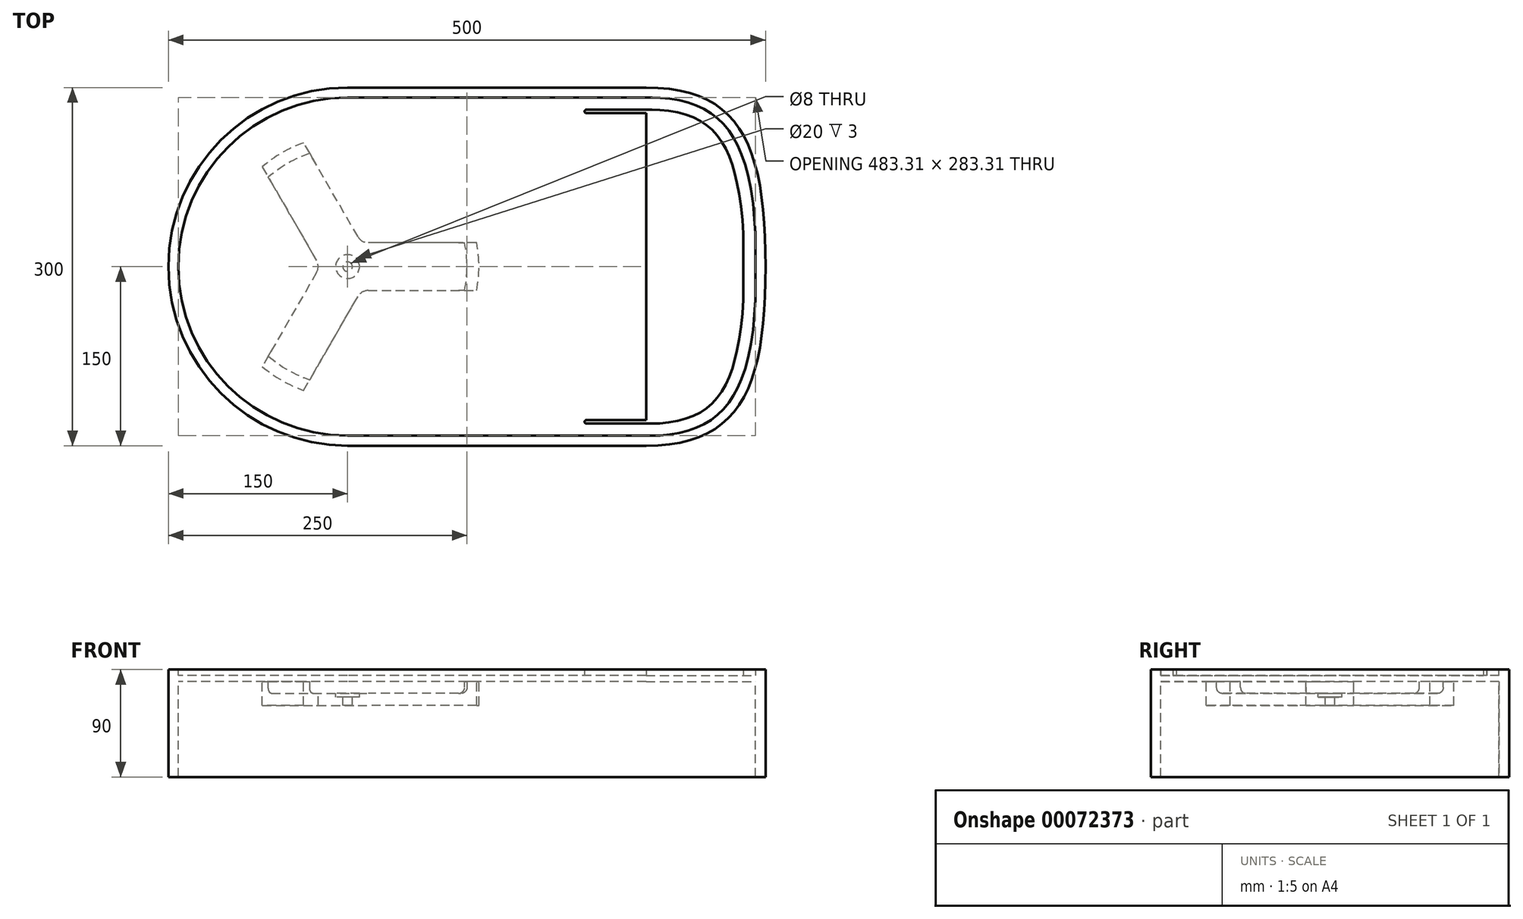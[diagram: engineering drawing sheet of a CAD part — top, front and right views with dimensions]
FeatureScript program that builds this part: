
annotation { "Feature Type Name" : "Feature", "Feature Type Description" : "" }
export const myFeature = defineFeature(function(context is Context, id is Id, definition is map)
    precondition{}
    {
        {
            var Q0;
            Q0=qCreatedBy(makeId("Top.planeOp"),FACE);
            var sketch = newSketch(context, id + "F0", { "sketchPlane" : qUnion([Q0])});
            skLineSegment(sketch, "E0.top", {"start": v(0, 150) * mm, "end": v(-250, 150) * mm});
            skArc(sketch, "E1", {"start": v(-250, 150) * mm, "mid": v(-356.07, 106.07) * mm, "end": v(-400, 0) * mm});
            skPoint(sketch, "E2", {"position": v(100, 0) * mm});
            skLineSegment(sketch, "E3", {"start": v(100, 0) * mm, "end": v(100, 200) * mm, "construction": true});
            skFitSpline(sketch, "E4", {"points": [v(0, 150) * mm, v(100, 0) * mm], "startDerivative": vector(240, 0) * mm, "endDerivative": vector(0, -300) * mm});
            skLineSegment(sketch, "E5", {"start": v(0, 150) * mm, "end": v(265.73, 150) * mm, "construction": true});
            skLineSegment(sketch, "E6", {"start": v(-400, 0) * mm, "end": v(100, 0) * mm, "construction": true});
            skArc(sketch, "E7.MirrorCS", {"start": v(-250, -150) * mm, "mid": v(-356.07, -106.07) * mm, "end": v(-400, 0) * mm});
            skLineSegment(sketch, "E8.MirrorCS", {"start": v(0, -150) * mm, "end": v(-250, -150) * mm});
            skFitSpline(sketch, "E9.MirrorCS", {"points": [v(0, -150) * mm, v(100, 0) * mm], "startDerivative": vector(240, 0) * mm, "endDerivative": vector(0, 300) * mm});
            skCircle(sketch, "E10", {"center": v(-250, 0) * mm, "radius": 110 * mm});
            skLineSegment(sketch, "E11.0", {"start": v(0, 130) * mm, "end": v(-250, 130) * mm, "construction": true});
            skFitSpline(sketch, "E11.1", {"points": [v(0, -130) * mm, v(4.48, -130) * mm, v(12.87, -129.65) * mm, v(23.79, -128.15) * mm, v(33.11, -125.8) * mm, v(40.98, -122.68) * mm, v(47.63, -118.88) * mm, v(53.34, -114.36) * mm, v(58.4, -108.95) * mm, v(62.93, -102.43) * mm, v(67, -94.6) * mm, v(70.55, -85.38) * mm, v(73.56, -74.7) * mm, v(76, -62.57) * mm, v(77.84, -49.03) * mm, v(79.54, -29.12) * mm, v(80, -12.17) * mm, v(80, 0) * mm], "construction": true});
            skLineSegment(sketch, "E11.2", {"start": v(0, -130) * mm, "end": v(-250, -130) * mm, "construction": true});
            skFitSpline(sketch, "E11.3", {"points": [v(0, 130) * mm, v(4.48, 130) * mm, v(12.87, 129.65) * mm, v(23.79, 128.15) * mm, v(33.11, 125.8) * mm, v(40.98, 122.68) * mm, v(47.63, 118.88) * mm, v(53.34, 114.36) * mm, v(58.4, 108.95) * mm, v(62.93, 102.43) * mm, v(67, 94.6) * mm, v(70.55, 85.38) * mm, v(73.56, 74.7) * mm, v(76, 62.57) * mm, v(77.84, 49.03) * mm, v(79.54, 29.12) * mm, v(80, 12.17) * mm, v(80, 0) * mm], "construction": true});
            skArc(sketch, "E11.4", {"start": v(-250, -130) * mm, "mid": v(-341.92, -91.92) * mm, "end": v(-380, 0) * mm, "construction": true});
            skArc(sketch, "E11.5", {"start": v(-250, 130) * mm, "mid": v(-341.92, 91.92) * mm, "end": v(-380, 0) * mm, "construction": true});
            skLineSegment(sketch, "E12", {"start": v(0, 130) * mm, "end": v(-50, 130) * mm, "construction": true});
            skLineSegment(sketch, "E13", {"start": v(-50, -150) * mm, "end": v(-50, 150) * mm, "construction": true});
            skLineSegment(sketch, "E14", {"start": v(-50, -130) * mm, "end": v(0, -130) * mm, "construction": true});
            skCircle(sketch, "E15", {"center": v(-250, 0) * mm, "radius": 100 * mm});
            skLineSegment(sketch, "E16.0", {"start": v(0, 141.65) * mm, "end": v(-250, 141.65) * mm});
            skFitSpline(sketch, "E16.1", {"points": [v(0, -141.65) * mm, v(4.78, -141.65) * mm, v(13.84, -141.28) * mm, v(25.94, -139.63) * mm, v(36.62, -136.94) * mm, v(45.99, -133.25) * mm, v(54.15, -128.6) * mm, v(61.28, -122.95) * mm, v(67.52, -116.25) * mm, v(72.97, -108.41) * mm, v(77.67, -99.34) * mm, v(82.97, -85.56) * mm, v(87.83, -65.1) * mm, v(91.04, -35.45) * mm, v(91.65, -12.36) * mm, v(91.65, 0) * mm]});
            skLineSegment(sketch, "E16.2", {"start": v(0, -141.65) * mm, "end": v(-250, -141.65) * mm});
            skFitSpline(sketch, "E16.3", {"points": [v(0, 141.65) * mm, v(4.78, 141.65) * mm, v(13.84, 141.28) * mm, v(25.94, 139.63) * mm, v(36.62, 136.94) * mm, v(45.99, 133.25) * mm, v(54.15, 128.6) * mm, v(61.28, 122.95) * mm, v(67.52, 116.25) * mm, v(72.97, 108.41) * mm, v(77.67, 99.34) * mm, v(82.97, 85.56) * mm, v(87.83, 65.1) * mm, v(91.04, 35.45) * mm, v(91.65, 12.36) * mm, v(91.65, 0) * mm]});
            skArc(sketch, "E16.4", {"start": v(-250, -141.65) * mm, "mid": v(-350.16, -100.16) * mm, "end": v(-391.65, 0) * mm});
            skArc(sketch, "E16.5", {"start": v(-250, 141.65) * mm, "mid": v(-350.16, 100.16) * mm, "end": v(-391.65, 0) * mm});
            skSolve(sketch);
        }
        {
            var Q0;
            Q0=makeQuery(id+"F0.imprint","IMPRINT",FACE,{"disambiguationData":[TD([[makeQuery(id+"F0.imprint","IMPRINT",EDGE,{"derivedFrom":sQuery(id+"F0.wireOp",EDGE,"E10")}),1.0]])]});
            var sketch = newSketch(context, id + "F1", { "sketchPlane" : qUnion([Q0])});
            skCircle(sketch, "E17", {"center": v(-250, 0) * mm, "radius": 130 * mm, "construction": true});
            skLineSegment(sketch, "E18", {"start": v(-130.42, 20) * mm, "end": v(-232.68, 20) * mm});
            skArc(sketch, "E19", {"start": v(-120.45, 10.83) * mm, "mid": v(-120, 0) * mm, "end": v(-120.45, -10.83) * mm});
            skLineSegment(sketch, "E20.1.0", {"start": v(-327.11, 93.56) * mm, "end": v(-275.98, 5) * mm});
            skArc(sketch, "E20.1.1", {"start": v(-324.16, 106.78) * mm, "mid": v(-315, 112.58) * mm, "end": v(-305.4, 117.6) * mm});
            skLineSegment(sketch, "E20.2.0", {"start": v(-292.47, -113.56) * mm, "end": v(-241.34, -25) * mm});
            skArc(sketch, "E20.2.1", {"start": v(-305.4, -117.6) * mm, "mid": v(-315, -112.58) * mm, "end": v(-324.16, -106.78) * mm});
            skLineSegment(sketch, "E21", {"start": v(-241.34, 25) * mm, "end": v(-292.47, 113.56) * mm});
            skLineSegment(sketch, "E22", {"start": v(-232.68, -20) * mm, "end": v(-130.42, -20) * mm});
            skLineSegment(sketch, "E23", {"start": v(-275.98, -5) * mm, "end": v(-327.11, -93.56) * mm});
            skPoint(sketch, "E24.visualSharp", {"position": v(-121.55, -20) * mm});
            skArc(sketch, "E24.filletArc", {"start": v(-130.42, -20) * mm, "mid": v(-123.65, -17.36) * mm, "end": v(-120.45, -10.83) * mm});
            skPoint(sketch, "E25.visualSharp", {"position": v(-121.55, 20) * mm});
            skArc(sketch, "E25.filletArc", {"start": v(-120.45, 10.83) * mm, "mid": v(-123.65, 17.36) * mm, "end": v(-130.42, 20) * mm});
            skPoint(sketch, "E26.visualSharp", {"position": v(-238.45, -20) * mm});
            skArc(sketch, "E26.filletArc", {"start": v(-232.68, -20) * mm, "mid": v(-237.68, -21.34) * mm, "end": v(-241.34, -25) * mm});
            skPoint(sketch, "E27.visualSharp", {"position": v(-238.45, 20) * mm});
            skArc(sketch, "E27.filletArc", {"start": v(-241.34, 25) * mm, "mid": v(-237.68, 21.34) * mm, "end": v(-232.68, 20) * mm});
            skPoint(sketch, "E28.visualSharp", {"position": v(-273.1, 0) * mm});
            skArc(sketch, "E28.filletArc", {"start": v(-275.98, -5) * mm, "mid": v(-274.64, 0) * mm, "end": v(-275.98, 5) * mm});
            skPoint(sketch, "E29.visualSharp", {"position": v(-296.9, 121.24) * mm});
            skArc(sketch, "E29.filletArc", {"start": v(-292.47, 113.56) * mm, "mid": v(-298.14, 118.1) * mm, "end": v(-305.4, 117.6) * mm});
            skPoint(sketch, "E30.visualSharp", {"position": v(-331.55, 101.24) * mm});
            skArc(sketch, "E30.filletArc", {"start": v(-324.16, 106.78) * mm, "mid": v(-328.21, 100.74) * mm, "end": v(-327.11, 93.56) * mm});
            skPoint(sketch, "E31.visualSharp", {"position": v(-296.9, -121.24) * mm});
            skArc(sketch, "E31.filletArc", {"start": v(-305.4, -117.6) * mm, "mid": v(-298.14, -118.1) * mm, "end": v(-292.47, -113.56) * mm});
            skPoint(sketch, "E32.visualSharp", {"position": v(-331.55, -101.24) * mm});
            skArc(sketch, "E32.filletArc", {"start": v(-327.11, -93.56) * mm, "mid": v(-328.21, -100.74) * mm, "end": v(-324.16, -106.78) * mm});
            skCircle(sketch, "E33", {"center": v(-250, 0) * mm, "radius": 10 * mm});
            skCircle(sketch, "E34", {"center": v(-250, 0) * mm, "radius": 4 * mm});
            skSolve(sketch);
        }
        {
            var Q0;
            Q0=makeQuery(id+"F0.imprint","IMPRINT",FACE,{"disambiguationData":[TD([[makeQuery(id+"F0.imprint","IMPRINT",EDGE,{"derivedFrom":sQuery(id+"F0.wireOp",EDGE,"E0.top")}),1.0]])]});
            var sketch = newSketch(context, id + "F2", { "sketchPlane" : qUnion([Q0])});
            skLineSegment(sketch, "E35", {"start": v(-50, -130) * mm, "end": v(0, -130) * mm, "construction": true});
            skFitSpline(sketch, "E36.1", {"points": [v(0, -130) * mm, v(4.48, -130) * mm, v(12.87, -129.65) * mm, v(23.79, -128.15) * mm, v(33.11, -125.8) * mm, v(40.98, -122.68) * mm, v(47.63, -118.88) * mm, v(53.34, -114.36) * mm, v(58.4, -108.95) * mm, v(62.93, -102.43) * mm, v(67, -94.6) * mm, v(70.55, -85.38) * mm, v(73.56, -74.7) * mm, v(76, -62.57) * mm, v(77.84, -49.03) * mm, v(79.54, -29.12) * mm, v(80, -12.17) * mm, v(80, 0) * mm], "construction": true});
            skFitSpline(sketch, "E36.3", {"points": [v(0, 130) * mm, v(4.48, 130) * mm, v(12.87, 129.65) * mm, v(23.79, 128.15) * mm, v(33.11, 125.8) * mm, v(40.98, 122.68) * mm, v(47.63, 118.88) * mm, v(53.34, 114.36) * mm, v(58.4, 108.95) * mm, v(62.93, 102.43) * mm, v(67, 94.6) * mm, v(70.55, 85.38) * mm, v(73.56, 74.7) * mm, v(76, 62.57) * mm, v(77.84, 49.03) * mm, v(79.54, 29.12) * mm, v(80, 12.17) * mm, v(80, 0) * mm], "construction": true});
            skLineSegment(sketch, "E37", {"start": v(0, 130) * mm, "end": v(-50, 130) * mm, "construction": true});
            skArc(sketch, "E38.0.startCap", {"start": v(-50, -131.5) * mm, "mid": v(-51.5, -130) * mm, "end": v(-50, -128.5) * mm});
            skLineSegment(sketch, "E38.0.left", {"start": v(-50, -128.5) * mm, "end": v(-3, -128.5) * mm});
            skLineSegment(sketch, "E38.0.right", {"start": v(-50, -131.5) * mm, "end": v(0, -131.5) * mm});
            skArc(sketch, "E38.1.endCap", {"start": v(-50, 128.5) * mm, "mid": v(-51.5, 130) * mm, "end": v(-50, 131.5) * mm});
            skLineSegment(sketch, "E38.1.left", {"start": v(0, 128.5) * mm, "end": v(-3, 128.5) * mm});
            skLineSegment(sketch, "E38.1.right", {"start": v(0, 131.5) * mm, "end": v(-50, 131.5) * mm});
            skFitSpline(sketch, "E38.2.left", {"points": [v(0, -128.5) * mm, v(4.44, -128.5) * mm, v(12.75, -128.15) * mm, v(23.51, -126.68) * mm, v(32.66, -124.36) * mm, v(40.34, -121.32) * mm, v(46.79, -117.63) * mm, v(52.32, -113.25) * mm, v(57.22, -108) * mm, v(61.64, -101.66) * mm, v(65.62, -94) * mm, v(69.12, -84.91) * mm, v(72.1, -74.36) * mm, v(74.51, -62.33) * mm, v(76.35, -48.87) * mm, v(78.04, -29.05) * mm, v(78.5, -12.14) * mm, v(78.5, 0) * mm]});
            skFitSpline(sketch, "E38.2.right", {"points": [v(0, -131.5) * mm, v(4.52, -131.5) * mm, v(13, -131.15) * mm, v(24.07, -129.63) * mm, v(33.56, -127.23) * mm, v(41.62, -124.04) * mm, v(48.47, -120.13) * mm, v(54.36, -115.46) * mm, v(59.57, -109.89) * mm, v(64.22, -103.2) * mm, v(68.37, -95.22) * mm, v(71.98, -85.85) * mm, v(75.02, -75.04) * mm, v(78.3, -58.74) * mm, v(80.89, -34.86) * mm, v(81.5, -12.2) * mm, v(81.5, 0) * mm]});
            skFitSpline(sketch, "E38.3.left", {"points": [v(0, 131.5) * mm, v(4.52, 131.5) * mm, v(13, 131.15) * mm, v(24.07, 129.63) * mm, v(33.56, 127.23) * mm, v(41.62, 124.04) * mm, v(48.47, 120.13) * mm, v(54.36, 115.46) * mm, v(59.57, 109.89) * mm, v(64.22, 103.2) * mm, v(68.37, 95.22) * mm, v(71.98, 85.85) * mm, v(75.02, 75.04) * mm, v(78.3, 58.74) * mm, v(80.89, 34.86) * mm, v(81.5, 12.2) * mm, v(81.5, 0) * mm]});
            skFitSpline(sketch, "E38.3.right", {"points": [v(0, 128.5) * mm, v(4.44, 128.5) * mm, v(12.75, 128.15) * mm, v(23.51, 126.68) * mm, v(32.66, 124.36) * mm, v(40.34, 121.32) * mm, v(46.79, 117.63) * mm, v(52.32, 113.25) * mm, v(57.22, 108) * mm, v(61.64, 101.66) * mm, v(65.62, 94) * mm, v(69.12, 84.91) * mm, v(72.1, 74.36) * mm, v(74.51, 62.33) * mm, v(76.35, 48.87) * mm, v(78.04, 29.05) * mm, v(78.5, 12.14) * mm, v(78.5, 0) * mm]});
            skLineSegment(sketch, "E39.left", {"start": v(0, -128.5) * mm, "end": v(0, 128.5) * mm});
            skLineSegment(sketch, "E39.right", {"start": v(-3, -128.5) * mm, "end": v(-3, 128.5) * mm});
            skLineSegment(sketch, "E40", {"start": v(-3, 128.5) * mm, "end": v(-50, 128.5) * mm});
            skLineSegment(sketch, "E41", {"start": v(0, -128.5) * mm, "end": v(-3, -128.5) * mm});
            skSolve(sketch);
        }
        {
            var Q0;
            Q0=makeQuery(id+"F0.imprint","IMPRINT",FACE,{"disambiguationData":[TD([[makeQuery(id+"F0.imprint","IMPRINT",EDGE,{"derivedFrom":sQuery(id+"F0.wireOp",EDGE,"E10")}),-1.0]])]});
            var Q1;
            Q1=makeQuery(id+"F0.imprint","IMPRINT",FACE,{"disambiguationData":[TD([[makeQuery(id+"F0.imprint","IMPRINT",EDGE,{"derivedFrom":sQuery(id+"F0.wireOp",EDGE,"E0.top")}),1.0]])]});
            extrude(context, id + "F3", {"entities" : qUnion([Q0, Q1]), "depth" : 10 * mm});
        }
        {
            var Q0;
            Q0=makeQuery(id+"F0.imprint","IMPRINT",FACE,{"disambiguationData":[TD([[makeQuery(id+"F0.imprint","IMPRINT",EDGE,{"derivedFrom":sQuery(id+"F0.wireOp",EDGE,"E10")}),1.0]])]});
            extrude(context, id + "F4", {"entities" : qUnion([Q0]), "operationType" : NewBodyOperationType.ADD, "depth" : 5 * mm});
        }
        {
            var Q0;
            Q0=makeQuery(id+"F0.imprint","IMPRINT",FACE,{"disambiguationData":[TD([[makeQuery(id+"F0.imprint","IMPRINT",EDGE,{"derivedFrom":sQuery(id+"F0.wireOp",EDGE,"E0.top")}),1.0]])]});
            extrude(context, id + "F5", {"entities" : qUnion([Q0]), "operationType" : NewBodyOperationType.ADD, "oppositeDirection" : true, "depth" : 80 * mm, "hasSecondDirection" : true, "secondDirectionOppositeDirection" : false, "secondDirectionDepth" : 1 * mm});
        }
        {
            var Q0;
            {var subQ0=sQuery(id+"F1.wireOp",EDGE,"E18");var subQ1=makeQuery(id+"F0.imprint","IMPRINT",EDGE,{"derivedFrom":sQuery(id+"F0.wireOp",EDGE,"E10")});var subQ2=makeQuery(id+"F1.imprint","INTERSECT",VERTEX,{"derivedFrom":[subQ1,subQ0]});Q0=makeQuery(id+"F1.imprint","IMPRINT",FACE,{"disambiguationData":[TD([[makeQuery(id+"F1.imprint","IMPRINT",EDGE,{"disambiguationData":[TD([[subQ2,-1.0]])],"derivedFrom":subQ0}),1.0]])]});}
            var Q1;
            Q1=makeQuery(id+"F1.imprint","IMPRINT",FACE,{"disambiguationData":[TD([[makeQuery(id+"F1.imprint","IMPRINT",EDGE,{"derivedFrom":sQuery(id+"F1.wireOp",EDGE,"E19")}),-1.0]])]});
            var Q2;
            {var subQ0=sQuery(id+"F1.wireOp",EDGE,"E20.1.0");var subQ1=makeQuery(id+"F0.imprint","IMPRINT",EDGE,{"derivedFrom":sQuery(id+"F0.wireOp",EDGE,"E10")});var subQ2=makeQuery(id+"F1.imprint","INTERSECT",VERTEX,{"derivedFrom":[subQ1,subQ0]});Q2=makeQuery(id+"F1.imprint","IMPRINT",FACE,{"disambiguationData":[TD([[makeQuery(id+"F1.imprint","IMPRINT",EDGE,{"disambiguationData":[TD([[subQ2,-1.0]])],"derivedFrom":subQ0}),1.0]])]});}
            var Q3;
            Q3=makeQuery(id+"F1.imprint","IMPRINT",FACE,{"disambiguationData":[TD([[makeQuery(id+"F1.imprint","IMPRINT",EDGE,{"derivedFrom":sQuery(id+"F1.wireOp",EDGE,"E20.1.1")}),-1.0]])]});
            var Q4;
            Q4=makeQuery(id+"F1.imprint","IMPRINT",FACE,{"disambiguationData":[TD([[makeQuery(id+"F1.imprint","IMPRINT",EDGE,{"derivedFrom":sQuery(id+"F1.wireOp",EDGE,"E20.2.1")}),-1.0]])]});
            var Q5;
            {var subQ0=sQuery(id+"F1.wireOp",EDGE,"E20.2.0");var subQ1=makeQuery(id+"F0.imprint","IMPRINT",EDGE,{"derivedFrom":sQuery(id+"F0.wireOp",EDGE,"E10")});var subQ2=makeQuery(id+"F1.imprint","INTERSECT",VERTEX,{"derivedFrom":[subQ1,subQ0]});Q5=makeQuery(id+"F1.imprint","IMPRINT",FACE,{"disambiguationData":[TD([[makeQuery(id+"F1.imprint","IMPRINT",EDGE,{"disambiguationData":[TD([[subQ2,-1.0]])],"derivedFrom":subQ0}),1.0]])]});}
            var Q6;
            {var subQ5=sQuery(id+"F1.wireOp",EDGE,"E26.filletArc");Q6=makeQuery(id+"F1.imprint","IMPRINT",FACE,{"disambiguationData":[TD([[makeQuery(id+"F1.imprint","IMPRINT",EDGE,{"derivedFrom":subQ5}),-1.0]])]});}
            var Q7;
            Q7=makeQuery(id+"F1.imprint","IMPRINT",FACE,{"disambiguationData":[TD([[makeQuery(id+"F1.imprint","IMPRINT",EDGE,{"derivedFrom":sQuery(id+"F1.wireOp",EDGE,"c12b578e-dc37-45e0-80c4-257baf1c9c70.0")}),-1.0]])]});
            var Q8;
            Q8=makeQuery(id+"F1.imprint","IMPRINT",FACE,{"disambiguationData":[TD([[makeQuery(id+"F1.imprint","IMPRINT",EDGE,{"derivedFrom":sQuery(id+"F1.wireOp",EDGE,"E33")}),1.0]])]});
            extrude(context, id + "F6", {"entities" : qUnion([Q0, Q1, Q2, Q3, Q4, Q5, Q6, Q7, Q8]), "operationType" : NewBodyOperationType.ADD, "oppositeDirection" : true, "depth" : 20 * mm});
        }
        {
            var Q0;
            {var subQ5=sQuery(id+"F1.wireOp",EDGE,"E26.filletArc");Q0=makeQuery(id+"F1.imprint","IMPRINT",FACE,{"disambiguationData":[TD([[makeQuery(id+"F1.imprint","IMPRINT",EDGE,{"derivedFrom":subQ5}),-1.0]])]});}
            var Q1;
            Q1=makeQuery(id+"F1.imprint","IMPRINT",FACE,{"disambiguationData":[TD([[makeQuery(id+"F1.imprint","IMPRINT",EDGE,{"derivedFrom":sQuery(id+"F1.wireOp",EDGE,"c12b578e-dc37-45e0-80c4-257baf1c9c70.0")}),-1.0]])]});
            extrude(context, id + "F7", {"entities" : qUnion([Q0, Q1]), "operationType" : NewBodyOperationType.REMOVE, "oppositeDirection" : true, "depth" : 10 * mm});
        }
        {
            var Q0;
            {var subQ3=sQuery(id+"F2.wireOp",EDGE,"E38.1.left");Q0=makeQuery(id+"F2.imprint","IMPRINT",FACE,{"disambiguationData":[TD([[makeQuery(id+"F2.imprint","IMPRINT",EDGE,{"derivedFrom":subQ3}),1.0]])]});}
            var Q1;
            Q1=makeQuery(id+"F2.imprint","IMPRINT",FACE,{"disambiguationData":[TD([[makeQuery(id+"F2.imprint","IMPRINT",EDGE,{"derivedFrom":sQuery(id+"F2.wireOp",EDGE,"E38.0.startCap")}),-1.0]])]});
            extrude(context, id + "F8", {"entities" : qUnion([Q0, Q1]), "operationType" : NewBodyOperationType.REMOVE, "endBound" : BoundingType.UP_TO_NEXT, "depth" : 25 * mm});
        }
        {
            var Q0;
            {var subQ3=sQuery(id+"F2.wireOp",EDGE,"E38.1.left");Q0=makeQuery(id+"F2.imprint","IMPRINT",FACE,{"disambiguationData":[TD([[makeQuery(id+"F2.imprint","IMPRINT",EDGE,{"derivedFrom":subQ3}),1.0]])]});}
            var Q1;
            Q1=makeQuery(id+"F2.imprint","IMPRINT",FACE,{"disambiguationData":[TD([[makeQuery(id+"F2.imprint","IMPRINT",EDGE,{"derivedFrom":sQuery(id+"F2.wireOp",EDGE,"E38.0.startCap")}),-1.0]])]});
            extrude(context, id + "F9", {"entities" : qUnion([Q0, Q1]), "operationType" : NewBodyOperationType.ADD, "depth" : 5 * mm});
        }
        {
            var Q0;
            {var subQ0=sQuery(id+"F0.wireOp",EDGE,"E15");var subQ1=makeQuery(id+"F0.imprint","IMPRINT",EDGE,{"derivedFrom":subQ0});Q0=makeQuery(id+"F7.boolean.opBoolean","COPY",EDGE,{"derivedFrom":makeQuery(id+"F7.opExtrude","CAP_EDGE",EDGE,{"disambiguationData":[OSD([subQ0]),TDD([makeQuery(id+"F1.imprint","IMPRINT",EDGE,{"disambiguationData":[TD([[makeQuery(id+"F1.imprint","INTERSECT",VERTEX,{"derivedFrom":[subQ1,sQuery(id+"F1.wireOp",EDGE,"E18")]}),1.0]])],"derivedFrom":subQ1})])],"isStart":false})});}
            var Q1;
            {var subQ0=sQuery(id+"F0.wireOp",EDGE,"E15");var subQ1=makeQuery(id+"F0.imprint","IMPRINT",EDGE,{"derivedFrom":subQ0});Q1=makeQuery(id+"F7.boolean.opBoolean","COPY",EDGE,{"derivedFrom":makeQuery(id+"F7.opExtrude","CAP_EDGE",EDGE,{"disambiguationData":[OSD([subQ0]),TDD([makeQuery(id+"F1.imprint","IMPRINT",EDGE,{"disambiguationData":[TD([[makeQuery(id+"F1.imprint","INTERSECT",VERTEX,{"derivedFrom":[subQ1,sQuery(id+"F1.wireOp",EDGE,"E20.1.0")]}),1.0]])],"derivedFrom":subQ1})])],"isStart":false})});}
            var Q2;
            {var subQ0=sQuery(id+"F0.wireOp",EDGE,"E15");var subQ1=makeQuery(id+"F0.imprint","IMPRINT",EDGE,{"derivedFrom":subQ0});Q2=makeQuery(id+"F7.boolean.opBoolean","COPY",EDGE,{"derivedFrom":makeQuery(id+"F7.opExtrude","CAP_EDGE",EDGE,{"disambiguationData":[OSD([subQ0]),TDD([makeQuery(id+"F1.imprint","IMPRINT",EDGE,{"disambiguationData":[TD([[makeQuery(id+"F1.imprint","INTERSECT",VERTEX,{"derivedFrom":[subQ1,sQuery(id+"F1.wireOp",EDGE,"E20.2.0")]}),1.0]])],"derivedFrom":subQ1})])],"isStart":false})});}
            fillet(context, id + "F10", {"entities" : qUnion([Q0, Q1, Q2]), "radius" : 5 * mm, "tangentPropagation" : true, "allowEdgeOverflow" : false});
        }
        {
            var Q0;
            Q0=makeQuery(id+"F1.imprint","IMPRINT",FACE,{"disambiguationData":[TD([[makeQuery(id+"F1.imprint","IMPRINT",EDGE,{"derivedFrom":sQuery(id+"F1.wireOp",EDGE,"E33")}),1.0]])]});
            extrude(context, id + "F11", {"entities" : qUnion([Q0]), "operationType" : NewBodyOperationType.REMOVE, "oppositeDirection" : true, "depth" : 13 * mm});
        }
    });
